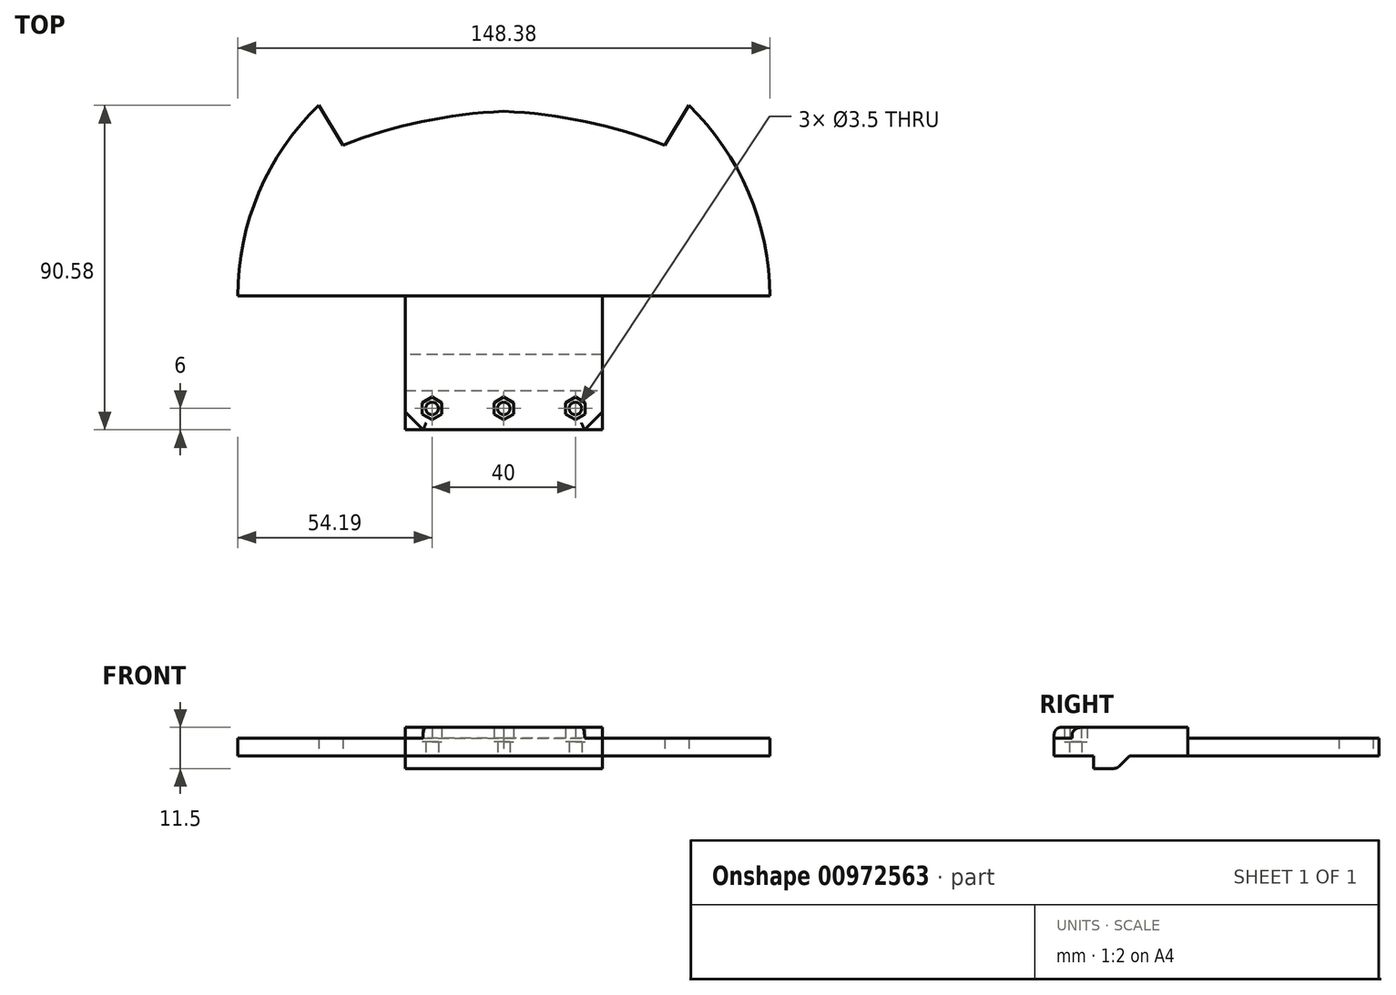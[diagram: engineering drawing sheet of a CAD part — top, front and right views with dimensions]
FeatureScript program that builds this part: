
annotation { "Feature Type Name" : "Feature", "Feature Type Description" : "" }
export const myFeature = defineFeature(function(context is Context, id is Id, definition is map)
    precondition{}
    {
        {
            assignVariable(context, id + "F0", {"name" : "TotalHeight", "anyValue" : 8});
        }
        {
            var Q0;
            Q0=qCreatedBy(makeId("Top.planeOp"),FACE);
            var sketch = newSketch(context, id + "F1", { "sketchPlane" : qUnion([Q0])});
            skCircle(sketch, "E0", {"center": v(0, -10) * mm, "radius": 1.75 * mm});
            skCircle(sketch, "E1", {"center": v(-20, -10) * mm, "radius": 1.75 * mm});
            skCircle(sketch, "E2", {"center": v(20, -10) * mm, "radius": 1.75 * mm});
            skLineSegment(sketch, "E3", {"start": v(0, -10) * mm, "end": v(-20, -10) * mm, "construction": true});
            skLineSegment(sketch, "E4", {"start": v(0, -10) * mm, "end": v(20, -10) * mm, "construction": true});
            skLineSegment(sketch, "E5", {"start": v(-27.5, 0) * mm, "end": v(27.5, 0) * mm});
            skLineSegment(sketch, "E6", {"start": v(-27.5, 0) * mm, "end": v(-27.5, -16) * mm});
            skLineSegment(sketch, "E7", {"start": v(-27.5, -16) * mm, "end": v(27.5, -16) * mm});
            skLineSegment(sketch, "E8", {"start": v(27.5, -16) * mm, "end": v(27.5, 0) * mm});
            skLineSegment(sketch, "E9", {"start": v(-27.5, -5) * mm, "end": v(27.5, -5) * mm});
            skCircle(sketch, "E10.cCircle", {"center": v(0, -10) * mm, "radius": 2.75 * mm, "construction": true});
            skLineSegment(sketch, "E10.0", {"start": v(-2.75, -11.59) * mm, "end": v(-2.75, -8.41) * mm});
            skLineSegment(sketch, "E10.1", {"start": v(-2.75, -8.41) * mm, "end": v(0, -6.82) * mm});
            skLineSegment(sketch, "E10.2", {"start": v(0, -6.82) * mm, "end": v(2.75, -8.41) * mm});
            skLineSegment(sketch, "E10.3", {"start": v(2.75, -8.41) * mm, "end": v(2.75, -11.59) * mm});
            skLineSegment(sketch, "E10.4", {"start": v(2.75, -11.59) * mm, "end": v(0, -13.18) * mm});
            skLineSegment(sketch, "E10.5", {"start": v(0, -13.18) * mm, "end": v(-2.75, -11.59) * mm});
            skPoint(sketch, "E10.0.midPoint", {"position": v(-2.75, -10) * mm});
            skCircle(sketch, "E11.cCircle", {"center": v(20, -10) * mm, "radius": 2.75 * mm, "construction": true});
            skLineSegment(sketch, "E11.0", {"start": v(17.25, -11.59) * mm, "end": v(17.25, -8.41) * mm});
            skLineSegment(sketch, "E11.1", {"start": v(17.25, -8.41) * mm, "end": v(20, -6.82) * mm});
            skLineSegment(sketch, "E11.2", {"start": v(20, -6.82) * mm, "end": v(22.75, -8.41) * mm});
            skLineSegment(sketch, "E11.3", {"start": v(22.75, -8.41) * mm, "end": v(22.75, -11.59) * mm});
            skLineSegment(sketch, "E11.4", {"start": v(22.75, -11.59) * mm, "end": v(20, -13.18) * mm});
            skLineSegment(sketch, "E11.5", {"start": v(20, -13.18) * mm, "end": v(17.25, -11.59) * mm});
            skPoint(sketch, "E11.0.midPoint", {"position": v(17.25, -10) * mm});
            skCircle(sketch, "E12.cCircle", {"center": v(-20, -10) * mm, "radius": 2.75 * mm, "construction": true});
            skLineSegment(sketch, "E12.0", {"start": v(-22.75, -11.59) * mm, "end": v(-22.75, -8.41) * mm});
            skLineSegment(sketch, "E12.1", {"start": v(-22.75, -8.41) * mm, "end": v(-20, -6.82) * mm});
            skLineSegment(sketch, "E12.2", {"start": v(-20, -6.82) * mm, "end": v(-17.25, -8.41) * mm});
            skLineSegment(sketch, "E12.3", {"start": v(-17.25, -8.41) * mm, "end": v(-17.25, -11.59) * mm});
            skLineSegment(sketch, "E12.4", {"start": v(-17.25, -11.59) * mm, "end": v(-20, -13.18) * mm});
            skLineSegment(sketch, "E12.5", {"start": v(-20, -13.18) * mm, "end": v(-22.75, -11.59) * mm});
            skPoint(sketch, "E12.0.midPoint", {"position": v(-22.75, -10) * mm});
            skLineSegment(sketch, "E13", {"start": v(-27.5, 0) * mm, "end": v(-27.5, 21.34) * mm});
            skLineSegment(sketch, "E14", {"start": v(27.5, 0) * mm, "end": v(27.5, 21.34) * mm});
            skLineSegment(sketch, "E15", {"start": v(-27.5, 21.34) * mm, "end": v(27.5, 21.34) * mm});
            skLineSegment(sketch, "E16", {"start": v(-27.5, 21.34) * mm, "end": v(-74.2, 21.34) * mm});
            skLineSegment(sketch, "E17.MirrorCS", {"start": v(27.5, 21.34) * mm, "end": v(74.2, 21.34) * mm});
            skArc(sketch, "E18", {"start": v(-51.61, 74.58) * mm, "mid": v(-68.32, 50.26) * mm, "end": v(-74.2, 21.34) * mm});
            skArc(sketch, "E19.MirrorCS", {"start": v(51.61, 74.58) * mm, "mid": v(68.32, 50.26) * mm, "end": v(74.2, 21.34) * mm});
            skLineSegment(sketch, "E20", {"start": v(-51.61, 74.58) * mm, "end": v(-44.92, 63.48) * mm});
            skArc(sketch, "E21", {"start": v(0, 72.92) * mm, "mid": v(-22.85, 70.04) * mm, "end": v(-44.92, 63.48) * mm});
            skArc(sketch, "E22.MirrorCS", {"start": v(0, 72.92) * mm, "mid": v(22.85, 70.04) * mm, "end": v(44.92, 63.48) * mm});
            skLineSegment(sketch, "E23.MirrorCS", {"start": v(51.61, 74.58) * mm, "end": v(44.92, 63.48) * mm});
            skSolve(sketch);
        }
        {
            var Q0;
            Q0=makeQuery(id+"F1.imprint","IMPRINT",FACE,{"disambiguationData":[TD([[makeQuery(id+"F1.imprint","IMPRINT",EDGE,{"derivedFrom":sQuery(id+"F1.wireOp",EDGE,"E5")}),1.0]])]});
            var Q1;
            {var subQ0=sQuery(id+"F1.wireOp",EDGE,"E5");Q1=makeQuery(id+"F1.imprint","IMPRINT",FACE,{"disambiguationData":[TD([[makeQuery(id+"F1.imprint","IMPRINT",EDGE,{"derivedFrom":subQ0}),-1.0]])]});}
            var Q2;
            {var subQ0=sQuery(id+"F1.wireOp",EDGE,"E7");Q2=makeQuery(id+"F1.imprint","IMPRINT",FACE,{"disambiguationData":[TD([[makeQuery(id+"F1.imprint","IMPRINT",EDGE,{"derivedFrom":subQ0}),1.0]])]});}
            var Q3;
            Q3=makeQuery(id+"F1.imprint","IMPRINT",FACE,{"disambiguationData":[TD([[makeQuery(id+"F1.imprint","IMPRINT",EDGE,{"derivedFrom":sQuery(id+"F1.wireOp",EDGE,"aea27d31-c2ea-4929-b87c-4423526370fa.0")}),1.0]])]});
            var Q4;
            Q4=makeQuery(id+"F1.imprint","IMPRINT",FACE,{"disambiguationData":[TD([[makeQuery(id+"F1.imprint","IMPRINT",EDGE,{"derivedFrom":sQuery(id+"F1.wireOp",EDGE,"E10.0")}),1.0]])]});
            extrude(context, id + "F2", {"entities" : qUnion([Q0, Q1, Q2, Q3, Q4]), "depth" : (getVariable(context, 'TotalHeight')) * mm, "offsetDistance" : 25 * mm});
        }
        {
            var Q0;
            Q0=makeQuery(id+"F1.imprint","IMPRINT",FACE,{"disambiguationData":[TD([[makeQuery(id+"F1.imprint","IMPRINT",EDGE,{"derivedFrom":sQuery(id+"F1.wireOp",EDGE,"E1")}),-1.0]])]});
            var Q1;
            Q1=makeQuery(id+"F1.imprint","IMPRINT",FACE,{"disambiguationData":[TD([[makeQuery(id+"F1.imprint","IMPRINT",EDGE,{"derivedFrom":sQuery(id+"F1.wireOp",EDGE,"E0")}),-1.0]])]});
            var Q2;
            Q2=makeQuery(id+"F1.imprint","IMPRINT",FACE,{"disambiguationData":[TD([[makeQuery(id+"F1.imprint","IMPRINT",EDGE,{"derivedFrom":sQuery(id+"F1.wireOp",EDGE,"E2")}),-1.0]])]});
            extrude(context, id + "F3", {"entities" : qUnion([Q0, Q1, Q2]), "operationType" : NewBodyOperationType.ADD, "depth" : (getVariable(context, 'TotalHeight') - 4) * mm, "offsetDistance" : 25 * mm});
        }
        {
            var Q0;
            {var subQ0=sQuery(id+"F1.wireOp",EDGE,"E5");Q0=makeQuery(id+"F1.imprint","IMPRINT",FACE,{"disambiguationData":[TD([[makeQuery(id+"F1.imprint","IMPRINT",EDGE,{"derivedFrom":subQ0}),-1.0]])]});}
            extrude(context, id + "F4", {"entities" : qUnion([Q0]), "operationType" : NewBodyOperationType.ADD, "oppositeDirection" : true, "depth" : 3.5 * mm, "offsetDistance" : 25 * mm});
        }
        {
            var Q0;
            Q0=makeQuery(id+"F2.opExtrude","SWEPT_EDGE",EDGE,{"disambiguationData":[OSD([sQuery(id+"F1.wireOp",EDGE,"E6"),sQuery(id+"F1.wireOp",EDGE,"E7")])]});
            var Q1;
            Q1=makeQuery(id+"F2.opExtrude","SWEPT_EDGE",EDGE,{"disambiguationData":[OSD([sQuery(id+"F1.wireOp",EDGE,"E7"),sQuery(id+"F1.wireOp",EDGE,"E8")])]});
            var Q2;
            Q2=makeQuery(id+"F4.opExtrude","CAP_EDGE",EDGE,{"disambiguationData":[OSD([sQuery(id+"F1.wireOp",EDGE,"E5")])],"isStart":true});
            chamfer(context, id + "F5", {"entities" : qUnion([Q0, Q1, Q2]), "width" : 5 * mm, "tangentPropagation" : true});
        }
        {
            var Q0;
            Q0=makeQuery(id+"F2.opExtrude","CAP_EDGE",EDGE,{"disambiguationData":[OSD([sQuery(id+"F1.wireOp",EDGE,"RsASE5nG-dPRU-RCI8-2qOx-PYFyHNF62bff")])],"isStart":true});
            var Q1;
            Q1=makeQuery(id+"F2.opExtrude","CAP_EDGE",EDGE,{"disambiguationData":[OSD([sQuery(id+"F1.wireOp",EDGE,"RsASE5nG-dPRU-RCI8-2qOx-PYFyHNF62bff")])],"isStart":false});
            var Q2;
            Q2=makeQuery(id+"F2.opExtrude","CAP_EDGE",EDGE,{"disambiguationData":[OSD([sQuery(id+"F1.wireOp",EDGE,"a3d60bbd-cd07-4952-b1fc-f427da875249.1")])],"isStart":true});
            var Q3;
            Q3=makeQuery(id+"F2.opExtrude","CAP_EDGE",EDGE,{"disambiguationData":[OSD([sQuery(id+"F1.wireOp",EDGE,"a3d60bbd-cd07-4952-b1fc-f427da875249.3")])],"isStart":false});
            var Q4;
            Q4=makeQuery(id+"F2.opExtrude","CAP_EDGE",EDGE,{"disambiguationData":[OSD([sQuery(id+"F1.wireOp",EDGE,"E7")])],"isStart":false});
            var Q5;
            {var subQ0=sQuery(id+"F1.wireOp",EDGE,"E7");var subQ1=sQuery(id+"F1.wireOp",EDGE,"E6");Q5=makeQuery(id+"F5.opChamfer","BLEND_EDGE",EDGE,{"blendedFrom":[makeQuery(id+"F4.boolean.opBoolean","MERGE",EDGE,{"derivedFrom":[makeQuery(id+"F2.opExtrude","SWEPT_EDGE",EDGE,{"disambiguationData":[OSD([subQ1,subQ0])]}),makeQuery(id+"F4.opExtrude","SWEPT_EDGE",EDGE,{"disambiguationData":[OSD([subQ1,subQ0])]})]}),makeQuery(id+"F2.opExtrude","CAP_FACE",FACE,{"disambiguationData":[OSD([subQ1,subQ0,sQuery(id+"F1.wireOp",EDGE,"E8"),sQuery(id+"F1.wireOp",EDGE,"aea27d31-c2ea-4929-b87c-4423526370fa.0"),sQuery(id+"F1.wireOp",EDGE,"aea27d31-c2ea-4929-b87c-4423526370fa.1"),sQuery(id+"F1.wireOp",EDGE,"aea27d31-c2ea-4929-b87c-4423526370fa.2"),sQuery(id+"F1.wireOp",EDGE,"aea27d31-c2ea-4929-b87c-4423526370fa.3"),sQuery(id+"F1.wireOp",EDGE,"aea27d31-c2ea-4929-b87c-4423526370fa.4"),sQuery(id+"F1.wireOp",EDGE,"aea27d31-c2ea-4929-b87c-4423526370fa.5"),sQuery(id+"F1.wireOp",EDGE,"E10.0"),sQuery(id+"F1.wireOp",EDGE,"E10.1"),sQuery(id+"F1.wireOp",EDGE,"E10.2"),sQuery(id+"F1.wireOp",EDGE,"E10.3"),sQuery(id+"F1.wireOp",EDGE,"E10.4"),sQuery(id+"F1.wireOp",EDGE,"E10.5"),sQuery(id+"F1.wireOp",EDGE,"E11.0"),sQuery(id+"F1.wireOp",EDGE,"E11.1"),sQuery(id+"F1.wireOp",EDGE,"E11.2"),sQuery(id+"F1.wireOp",EDGE,"E11.3"),sQuery(id+"F1.wireOp",EDGE,"E11.4"),sQuery(id+"F1.wireOp",EDGE,"E11.5"),sQuery(id+"F1.wireOp",EDGE,"RsASE5nG-dPRU-RCI8-2qOx-PYFyHNF62bff"),sQuery(id+"F1.wireOp",EDGE,"eb05861e-74fa-4697-aaf9-f4aa3c3135bf0.MirrorCS"),sQuery(id+"F1.wireOp",EDGE,"gBohGyNM-2VbG-c7K3-CVnN-0ivdIRm1ajVN"),sQuery(id+"F1.wireOp",EDGE,"a3d60bbd-cd07-4952-b1fc-f427da875249.0"),sQuery(id+"F1.wireOp",EDGE,"a3d60bbd-cd07-4952-b1fc-f427da875249.1"),sQuery(id+"F1.wireOp",EDGE,"a3d60bbd-cd07-4952-b1fc-f427da875249.2"),sQuery(id+"F1.wireOp",EDGE,"a3d60bbd-cd07-4952-b1fc-f427da875249.3")])],"isStart":false})],"blendedInto":[makeQuery(id+"F2.opExtrude","CAP_FACE",FACE,{"disambiguationData":[OSD([subQ1,subQ0,sQuery(id+"F1.wireOp",EDGE,"E8"),sQuery(id+"F1.wireOp",EDGE,"aea27d31-c2ea-4929-b87c-4423526370fa.0"),sQuery(id+"F1.wireOp",EDGE,"aea27d31-c2ea-4929-b87c-4423526370fa.1"),sQuery(id+"F1.wireOp",EDGE,"aea27d31-c2ea-4929-b87c-4423526370fa.2"),sQuery(id+"F1.wireOp",EDGE,"aea27d31-c2ea-4929-b87c-4423526370fa.3"),sQuery(id+"F1.wireOp",EDGE,"aea27d31-c2ea-4929-b87c-4423526370fa.4"),sQuery(id+"F1.wireOp",EDGE,"aea27d31-c2ea-4929-b87c-4423526370fa.5"),sQuery(id+"F1.wireOp",EDGE,"E10.0"),sQuery(id+"F1.wireOp",EDGE,"E10.1"),sQuery(id+"F1.wireOp",EDGE,"E10.2"),sQuery(id+"F1.wireOp",EDGE,"E10.3"),sQuery(id+"F1.wireOp",EDGE,"E10.4"),sQuery(id+"F1.wireOp",EDGE,"E10.5"),sQuery(id+"F1.wireOp",EDGE,"E11.0"),sQuery(id+"F1.wireOp",EDGE,"E11.1"),sQuery(id+"F1.wireOp",EDGE,"E11.2"),sQuery(id+"F1.wireOp",EDGE,"E11.3"),sQuery(id+"F1.wireOp",EDGE,"E11.4"),sQuery(id+"F1.wireOp",EDGE,"E11.5"),sQuery(id+"F1.wireOp",EDGE,"RsASE5nG-dPRU-RCI8-2qOx-PYFyHNF62bff"),sQuery(id+"F1.wireOp",EDGE,"eb05861e-74fa-4697-aaf9-f4aa3c3135bf0.MirrorCS"),sQuery(id+"F1.wireOp",EDGE,"gBohGyNM-2VbG-c7K3-CVnN-0ivdIRm1ajVN"),sQuery(id+"F1.wireOp",EDGE,"a3d60bbd-cd07-4952-b1fc-f427da875249.0"),sQuery(id+"F1.wireOp",EDGE,"a3d60bbd-cd07-4952-b1fc-f427da875249.1"),sQuery(id+"F1.wireOp",EDGE,"a3d60bbd-cd07-4952-b1fc-f427da875249.2"),sQuery(id+"F1.wireOp",EDGE,"a3d60bbd-cd07-4952-b1fc-f427da875249.3")])],"isStart":false})]});}
            var Q6;
            {var subQ0=sQuery(id+"F1.wireOp",EDGE,"E8");var subQ1=sQuery(id+"F1.wireOp",EDGE,"E7");Q6=makeQuery(id+"F5.opChamfer","BLEND_EDGE",EDGE,{"blendedFrom":[makeQuery(id+"F4.boolean.opBoolean","MERGE",EDGE,{"derivedFrom":[makeQuery(id+"F2.opExtrude","SWEPT_EDGE",EDGE,{"disambiguationData":[OSD([subQ1,subQ0])]}),makeQuery(id+"F4.opExtrude","SWEPT_EDGE",EDGE,{"disambiguationData":[OSD([subQ1,subQ0])]})]}),makeQuery(id+"F2.opExtrude","CAP_FACE",FACE,{"disambiguationData":[OSD([sQuery(id+"F1.wireOp",EDGE,"E6"),subQ1,subQ0,sQuery(id+"F1.wireOp",EDGE,"aea27d31-c2ea-4929-b87c-4423526370fa.0"),sQuery(id+"F1.wireOp",EDGE,"aea27d31-c2ea-4929-b87c-4423526370fa.1"),sQuery(id+"F1.wireOp",EDGE,"aea27d31-c2ea-4929-b87c-4423526370fa.2"),sQuery(id+"F1.wireOp",EDGE,"aea27d31-c2ea-4929-b87c-4423526370fa.3"),sQuery(id+"F1.wireOp",EDGE,"aea27d31-c2ea-4929-b87c-4423526370fa.4"),sQuery(id+"F1.wireOp",EDGE,"aea27d31-c2ea-4929-b87c-4423526370fa.5"),sQuery(id+"F1.wireOp",EDGE,"E10.0"),sQuery(id+"F1.wireOp",EDGE,"E10.1"),sQuery(id+"F1.wireOp",EDGE,"E10.2"),sQuery(id+"F1.wireOp",EDGE,"E10.3"),sQuery(id+"F1.wireOp",EDGE,"E10.4"),sQuery(id+"F1.wireOp",EDGE,"E10.5"),sQuery(id+"F1.wireOp",EDGE,"E11.0"),sQuery(id+"F1.wireOp",EDGE,"E11.1"),sQuery(id+"F1.wireOp",EDGE,"E11.2"),sQuery(id+"F1.wireOp",EDGE,"E11.3"),sQuery(id+"F1.wireOp",EDGE,"E11.4"),sQuery(id+"F1.wireOp",EDGE,"E11.5"),sQuery(id+"F1.wireOp",EDGE,"RsASE5nG-dPRU-RCI8-2qOx-PYFyHNF62bff"),sQuery(id+"F1.wireOp",EDGE,"eb05861e-74fa-4697-aaf9-f4aa3c3135bf0.MirrorCS"),sQuery(id+"F1.wireOp",EDGE,"gBohGyNM-2VbG-c7K3-CVnN-0ivdIRm1ajVN"),sQuery(id+"F1.wireOp",EDGE,"a3d60bbd-cd07-4952-b1fc-f427da875249.0"),sQuery(id+"F1.wireOp",EDGE,"a3d60bbd-cd07-4952-b1fc-f427da875249.1"),sQuery(id+"F1.wireOp",EDGE,"a3d60bbd-cd07-4952-b1fc-f427da875249.2"),sQuery(id+"F1.wireOp",EDGE,"a3d60bbd-cd07-4952-b1fc-f427da875249.3")])],"isStart":false})],"blendedInto":[makeQuery(id+"F2.opExtrude","CAP_FACE",FACE,{"disambiguationData":[OSD([sQuery(id+"F1.wireOp",EDGE,"E6"),subQ1,subQ0,sQuery(id+"F1.wireOp",EDGE,"aea27d31-c2ea-4929-b87c-4423526370fa.0"),sQuery(id+"F1.wireOp",EDGE,"aea27d31-c2ea-4929-b87c-4423526370fa.1"),sQuery(id+"F1.wireOp",EDGE,"aea27d31-c2ea-4929-b87c-4423526370fa.2"),sQuery(id+"F1.wireOp",EDGE,"aea27d31-c2ea-4929-b87c-4423526370fa.3"),sQuery(id+"F1.wireOp",EDGE,"aea27d31-c2ea-4929-b87c-4423526370fa.4"),sQuery(id+"F1.wireOp",EDGE,"aea27d31-c2ea-4929-b87c-4423526370fa.5"),sQuery(id+"F1.wireOp",EDGE,"E10.0"),sQuery(id+"F1.wireOp",EDGE,"E10.1"),sQuery(id+"F1.wireOp",EDGE,"E10.2"),sQuery(id+"F1.wireOp",EDGE,"E10.3"),sQuery(id+"F1.wireOp",EDGE,"E10.4"),sQuery(id+"F1.wireOp",EDGE,"E10.5"),sQuery(id+"F1.wireOp",EDGE,"E11.0"),sQuery(id+"F1.wireOp",EDGE,"E11.1"),sQuery(id+"F1.wireOp",EDGE,"E11.2"),sQuery(id+"F1.wireOp",EDGE,"E11.3"),sQuery(id+"F1.wireOp",EDGE,"E11.4"),sQuery(id+"F1.wireOp",EDGE,"E11.5"),sQuery(id+"F1.wireOp",EDGE,"RsASE5nG-dPRU-RCI8-2qOx-PYFyHNF62bff"),sQuery(id+"F1.wireOp",EDGE,"eb05861e-74fa-4697-aaf9-f4aa3c3135bf0.MirrorCS"),sQuery(id+"F1.wireOp",EDGE,"gBohGyNM-2VbG-c7K3-CVnN-0ivdIRm1ajVN"),sQuery(id+"F1.wireOp",EDGE,"a3d60bbd-cd07-4952-b1fc-f427da875249.0"),sQuery(id+"F1.wireOp",EDGE,"a3d60bbd-cd07-4952-b1fc-f427da875249.1"),sQuery(id+"F1.wireOp",EDGE,"a3d60bbd-cd07-4952-b1fc-f427da875249.2"),sQuery(id+"F1.wireOp",EDGE,"a3d60bbd-cd07-4952-b1fc-f427da875249.3")])],"isStart":false})]});}
            var Q7;
            Q7=makeQuery(id+"F5.opChamfer","BLEND_EDGE",EDGE,{"blendedFrom":[makeQuery(id+"F4.opExtrude","CAP_EDGE",EDGE,{"disambiguationData":[OSD([sQuery(id+"F1.wireOp",EDGE,"E5")])],"isStart":true}),makeQuery(id+"F2.opExtrude","SWEPT_FACE",FACE,{"disambiguationData":[OSD([sQuery(id+"F1.wireOp",EDGE,"eb05861e-74fa-4697-aaf9-f4aa3c3135bf0.MirrorCS")])]})],"blendedInto":[makeQuery(id+"F2.opExtrude","SWEPT_FACE",FACE,{"disambiguationData":[OSD([sQuery(id+"F1.wireOp",EDGE,"eb05861e-74fa-4697-aaf9-f4aa3c3135bf0.MirrorCS")])]})]});
            var Q8;
            Q8=makeQuery(id+"F5.opChamfer","BLEND_EDGE",EDGE,{"blendedFrom":[makeQuery(id+"F4.opExtrude","CAP_EDGE",EDGE,{"disambiguationData":[OSD([sQuery(id+"F1.wireOp",EDGE,"E5")])],"isStart":true}),makeQuery(id+"F2.opExtrude","SWEPT_FACE",FACE,{"disambiguationData":[OSD([sQuery(id+"F1.wireOp",EDGE,"RsASE5nG-dPRU-RCI8-2qOx-PYFyHNF62bff")])]})],"blendedInto":[makeQuery(id+"F2.opExtrude","SWEPT_FACE",FACE,{"disambiguationData":[OSD([sQuery(id+"F1.wireOp",EDGE,"RsASE5nG-dPRU-RCI8-2qOx-PYFyHNF62bff")])]})]});
            var Q9;
            Q9=makeQuery(id+"F5.opChamfer","BLEND_EDGE",EDGE,{"blendedFrom":[makeQuery(id+"F4.opExtrude","CAP_EDGE",EDGE,{"disambiguationData":[OSD([sQuery(id+"F1.wireOp",EDGE,"E5")])],"isStart":true}),makeQuery(id+"F2.opExtrude","SWEPT_FACE",FACE,{"disambiguationData":[OSD([sQuery(id+"F1.wireOp",EDGE,"a3d60bbd-cd07-4952-b1fc-f427da875249.2")])]})],"blendedInto":[makeQuery(id+"F2.opExtrude","SWEPT_FACE",FACE,{"disambiguationData":[OSD([sQuery(id+"F1.wireOp",EDGE,"a3d60bbd-cd07-4952-b1fc-f427da875249.2")])]})]});
            var Q10;
            {var subQ0=sQuery(id+"F1.wireOp",EDGE,"E5");Q10=makeQuery(id+"F5.opChamfer","BLEND_EDGE",EDGE,{"blendedFrom":[makeQuery(id+"F4.opExtrude","CAP_EDGE",EDGE,{"disambiguationData":[OSD([subQ0])],"isStart":true}),makeQuery(id+"F4.opExtrude","CAP_FACE",FACE,{"disambiguationData":[OSD([subQ0,sQuery(id+"F1.wireOp",EDGE,"E6"),sQuery(id+"F1.wireOp",EDGE,"E7"),sQuery(id+"F1.wireOp",EDGE,"E8"),sQuery(id+"F1.wireOp",EDGE,"E9"),sQuery(id+"F1.wireOp",EDGE,"82qEuTwf-rWpJ-iMl8-XhDT-ZZMlZaatkq3s.left"),sQuery(id+"F1.wireOp",EDGE,"82qEuTwf-rWpJ-iMl8-XhDT-ZZMlZaatkq3s.right")])],"isStart":false})],"blendedInto":[makeQuery(id+"F4.opExtrude","CAP_FACE",FACE,{"disambiguationData":[OSD([subQ0,sQuery(id+"F1.wireOp",EDGE,"E6"),sQuery(id+"F1.wireOp",EDGE,"E7"),sQuery(id+"F1.wireOp",EDGE,"E8"),sQuery(id+"F1.wireOp",EDGE,"E9"),sQuery(id+"F1.wireOp",EDGE,"82qEuTwf-rWpJ-iMl8-XhDT-ZZMlZaatkq3s.left"),sQuery(id+"F1.wireOp",EDGE,"82qEuTwf-rWpJ-iMl8-XhDT-ZZMlZaatkq3s.right")])],"isStart":false})]});}
            fillet(context, id + "F6", {"entities" : qUnion([Q0, Q1, Q2, Q3, Q4, Q5, Q6, Q7, Q8, Q9, Q10]), "radius" : 2 * mm, "tangentPropagation" : true, "allowEdgeOverflow" : false});
        }
        {
            var Q0;
            Q0 = qSketchRegion(id + "F1", true);
            extrude(context, id + "F7", {"entities" : qUnion([Q0]), "operationType" : NewBodyOperationType.ADD, "depth" : 5 * mm, "offsetDistance" : 25 * mm});
        }
    });
